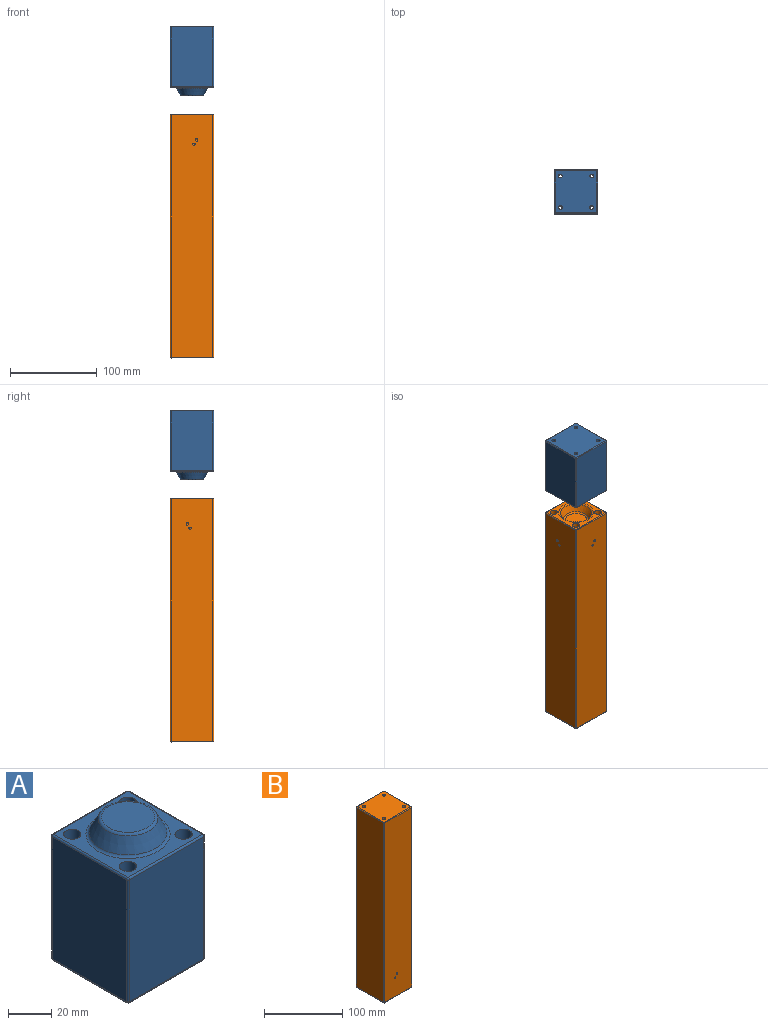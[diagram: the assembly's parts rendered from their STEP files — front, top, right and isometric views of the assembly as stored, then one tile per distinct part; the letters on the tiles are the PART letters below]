
ASSEMBLY  parts=2 mates=1
PART A: 42 faces, bbox 50.5x50.5x80.8 mm
  f0: plane 69x48.5mm, normal (0,1,0), area 3346.5mm2, adj f15,f24,f25,f29
  f1: plane 69x48.5mm, normal (-1,0,0), area 3346.5mm2, adj f18,f23,f26,f29
  f2: plane 69x48.5mm, normal (0,-1,0), area 3346.5mm2, adj f10,f13,f17,f18
  f3: plane 69x48.5mm, normal (1,0,0), area 3346.5mm2, adj f10,f14,f15,f16
  f4: plane 48.5x48.5mm, normal (0,0,-1), area 2288.6mm2, adj f13,f14,f23,f24,f30,f33,f36,f39
  f5: plane 48.5x48.5mm, normal (0,0,1), area 963.4mm2, adj f8,f16,f17,f25,f26,f32,f35,f38
  f6: cone r=13.38mm half-angle=27.1deg, axis (0,0,-1), area 879.6mm2, adj f8,f9
  f7: plane 24.61x24.61mm, normal (0,0,1), area 475.7mm2, adj f9
  f8: torus R=19.44mm, axis (0,0,1), area 224.1mm2, adj f5,f6
  f9: torus R=12.31mm, axis (0,0,1), area 158.9mm2, adj f6,f7
  f10: cylinder r=1mm len=69mm, axis (0,0,-1), area 108.4mm2, adj f2,f3,f11,f12
  f11: sphere r=1mm, area 1.6mm2, adj f10,f13,f14
  f12: sphere r=1mm, area 1.6mm2, adj f10,f16,f17
  f13: cylinder r=1mm len=48.5mm, axis (-1,0,0), area 76.2mm2, adj f2,f4,f11,f19
  f14: cylinder r=1mm len=48.5mm, axis (0,-1,0), area 76.2mm2, adj f3,f4,f11,f20
  f15: cylinder r=1mm len=69mm, axis (0,0,1), area 108.4mm2, adj f0,f3,f20,f21
  f16: cylinder r=1mm len=48.5mm, axis (0,1,0), area 76.2mm2, adj f3,f5,f12,f21
  f17: cylinder r=1mm len=48.5mm, axis (1,0,0), area 76.2mm2, adj f2,f5,f12,f22
  f18: cylinder r=1mm len=69mm, axis (0,0,1), area 108.4mm2, adj f1,f2,f19,f22
  f19: sphere r=1mm, area 1.6mm2, adj f13,f18,f23
  f20: sphere r=1mm, area 1.6mm2, adj f14,f15,f24
  f21: sphere r=1mm, area 1.6mm2, adj f15,f16,f25
  f22: sphere r=1mm, area 1.6mm2, adj f17,f18,f26
  f23: cylinder r=1mm len=48.5mm, axis (0,1,0), area 76.2mm2, adj f1,f4,f19,f27
  f24: cylinder r=1mm len=48.5mm, axis (1,0,0), area 76.2mm2, adj f0,f4,f20,f27
  f25: cylinder r=1mm len=48.5mm, axis (-1,0,0), area 76.2mm2, adj f0,f5,f21,f28
  f26: cylinder r=1mm len=48.5mm, axis (0,-1,0), area 76.2mm2, adj f1,f5,f22,f28
  f27: sphere r=1mm, area 1.6mm2, adj f23,f24,f29
  f28: sphere r=1mm, area 1.6mm2, adj f25,f26,f29
  f29: cylinder r=1mm len=69mm, axis (0,0,-1), area 108.4mm2, adj f0,f1,f27,f28
  f30: cylinder r=2.25mm len=4.5mm, axis (0,0,1), area 49.5mm2, adj f4,f31
  f31: plane 8x8mm, normal (0,0,1), area 34.4mm2, adj f30,f32
  f32: cylinder r=4mm len=67.5mm, axis (0,0,1), area 1696.5mm2, adj f5,f31
  f33: cylinder r=2.25mm len=4.5mm, axis (0,0,1), area 49.5mm2, adj f4,f34
  f34: plane 8x8mm, normal (0,0,1), area 34.4mm2, adj f33,f35
  f35: cylinder r=4mm len=67.5mm, axis (0,0,1), area 1696.5mm2, adj f5,f34
  f36: cylinder r=2.25mm len=4.5mm, axis (0,0,1), area 49.5mm2, adj f4,f37
  f37: plane 8x8mm, normal (0,0,1), area 34.4mm2, adj f36,f38
  f38: cylinder r=4mm len=67.5mm, axis (0,0,1), area 1696.5mm2, adj f5,f37
  f39: cylinder r=2.25mm len=4.5mm, axis (0,0,1), area 49.5mm2, adj f4,f40
  f40: plane 8x8mm, normal (0,0,1), area 34.4mm2, adj f39,f41
  f41: cylinder r=4mm len=67.5mm, axis (0,0,1), area 1696.5mm2, adj f5,f40
PART B: 50 faces, bbox 50.5x50.5x282 mm
  f0: plane 280x48.5mm, normal (0,1,0), area 13580mm2, adj f18,f23,f26,f29
  f1: plane 280x48.5mm, normal (-1,0,0), area 13580mm2, adj f15,f24,f25,f29
  f2: plane 280x48.5mm, normal (0,-1,0), area 13568.5mm2, adj f10,f14,f15,f16,f47,f49
  f3: plane 280x48.5mm, normal (1,0,0), area 13568.5mm2, adj f10,f13,f17,f18,f43,f45
  f4: plane 48.5x48.5mm, normal (0,0,1), area 2288.6mm2, adj f13,f14,f23,f24,f30,f33,f36,f39
  f5: plane 48.5x48.5mm, normal (0,0,-1), area 890.7mm2, adj f8,f16,f17,f25,f26,f32,f35,f38
  f6: cone r=18.62mm half-angle=26deg, axis (0,0,-1), area 870.6mm2, adj f8,f9
  f7: plane 24.44x24.44mm, normal (0,0,-1), area 469.1mm2, adj f9
  f8: torus R=20.03mm, axis (0,0,1), area 298.4mm2, adj f5,f6
  f9: torus R=12.22mm, axis (0,0,-1), area 210.8mm2, adj f6,f7
  f10: cylinder r=1mm len=280mm, axis (0,0,1), area 439.8mm2, adj f2,f3,f11,f12
  f11: sphere r=1mm, area 1.6mm2, adj f10,f13,f14
  f12: sphere r=1mm, area 1.6mm2, adj f10,f16,f17
  f13: cylinder r=1mm len=48.5mm, axis (0,-1,0), area 76.2mm2, adj f3,f4,f11,f19
  f14: cylinder r=1mm len=48.5mm, axis (-1,0,0), area 76.2mm2, adj f2,f4,f11,f20
  f15: cylinder r=1mm len=280mm, axis (0,0,-1), area 439.8mm2, adj f1,f2,f20,f21
  f16: cylinder r=1mm len=48.5mm, axis (1,0,0), area 76.2mm2, adj f2,f5,f12,f21
  f17: cylinder r=1mm len=48.5mm, axis (0,1,0), area 76.2mm2, adj f3,f5,f12,f22
  f18: cylinder r=1mm len=280mm, axis (0,0,-1), area 439.8mm2, adj f0,f3,f19,f22
  f19: sphere r=1mm, area 1.6mm2, adj f13,f18,f23
  f20: sphere r=1mm, area 1.6mm2, adj f14,f15,f24
  f21: sphere r=1mm, area 1.6mm2, adj f15,f16,f25
  f22: sphere r=1mm, area 1.6mm2, adj f17,f18,f26
  f23: cylinder r=1mm len=48.5mm, axis (1,0,0), area 76.2mm2, adj f0,f4,f19,f27
  f24: cylinder r=1mm len=48.5mm, axis (0,1,0), area 76.2mm2, adj f1,f4,f20,f27
  f25: cylinder r=1mm len=48.5mm, axis (0,-1,0), area 76.2mm2, adj f1,f5,f21,f28
  f26: cylinder r=1mm len=48.5mm, axis (-1,0,0), area 76.2mm2, adj f0,f5,f22,f28
  f27: sphere r=1mm, area 1.6mm2, adj f23,f24,f29
  f28: sphere r=1mm, area 1.6mm2, adj f25,f26,f29
  f29: cylinder r=1mm len=280mm, axis (0,0,1), area 439.8mm2, adj f0,f1,f27,f28
  f30: cylinder r=2.25mm len=4.5mm, axis (0,0,-1), area 49.5mm2, adj f4,f31
  f31: plane 8x8mm, normal (0,0,-1), area 34.4mm2, adj f30,f32
  f32: cylinder r=4mm len=278.5mm, axis (0,0,-1), area 6999.5mm2, adj f5,f31
  f33: cylinder r=2.25mm len=4.5mm, axis (0,0,-1), area 49.5mm2, adj f4,f34
  f34: plane 8x8mm, normal (0,0,-1), area 34.4mm2, adj f33,f35
  f35: cylinder r=4mm len=278.5mm, axis (0,0,-1), area 6999.5mm2, adj f5,f34
  f36: cylinder r=2.25mm len=4.5mm, axis (0,0,-1), area 49.5mm2, adj f4,f37
  f37: plane 8x8mm, normal (0,0,-1), area 34.4mm2, adj f36,f38
  f38: cylinder r=4mm len=278.5mm, axis (0,0,-1), area 6999.5mm2, adj f5,f37
  f39: cylinder r=2.25mm len=4.5mm, axis (0,0,-1), area 49.5mm2, adj f4,f40
  f40: plane 8x8mm, normal (0,0,-1), area 34.4mm2, adj f39,f41
  f41: cylinder r=4mm len=278.5mm, axis (0,0,-1), area 6999.5mm2, adj f5,f40
  f42: cone r=0mm half-angle=59deg, axis (1,0,0), area 6.7mm2, adj f43
  f43: cylinder r=1.35mm len=25mm, axis (1,0,0), area 212.1mm2, adj f3,f42
  f44: cone r=0mm half-angle=59deg, axis (1,0,0), area 6.7mm2, adj f45
  f45: cylinder r=1.35mm len=25mm, axis (1,0,0), area 212.1mm2, adj f3,f44
  f46: cone r=0mm half-angle=59deg, axis (0,-1,0), area 6.7mm2, adj f47
  f47: cylinder r=1.35mm len=25mm, axis (0,-1,0), area 212.1mm2, adj f2,f46
  f48: cone r=0mm half-angle=59deg, axis (0,-1,0), area 6.7mm2, adj f49
  f49: cylinder r=1.35mm len=25mm, axis (0,-1,0), area 212.1mm2, adj f2,f48
PLACE A rot(axis=(0,1,0),180deg) t=(112.52,34.23,160.49)mm
PLACE B rot(axis=(0,1,0),180deg) t=(112.52,34.23,159.73)mm
MATE slider A.f6 <-> B.f6  axis (0,0,1) through (87.27,8.98,180.74)mm
